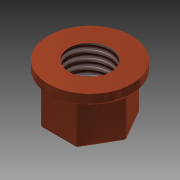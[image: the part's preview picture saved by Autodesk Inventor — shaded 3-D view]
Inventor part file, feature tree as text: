
AUTODESK INVENTOR PART (.ipt)
format: ipt  version: 2015 (Build 190159000, 159)  size: 140,800 bytes
history: native  units: mm
features: extrude x2, sketch x2, thread x1, fillet x1, chamfer x1
ambient origin geometry x8: Origin, YZ Plane, XZ Plane, XY Plane, X Axis, Y Axis, Z Axis, Center Point
bodies: 实体1 (feature_tree)
feature tree (7):
  extrude  "拉伸1"  Depth=4.0mm
  extrude  "拉伸2"  Depth=4.0mm TaperAngle=0.0deg
  thread  "螺纹1"  [1 undecoded]
  fillet  "圆角1"  Radius=4.0mm
  chamfer  "倒角1"  Distance=1.0mm
  sketch  "草图1"  dims[d0=4.0mm d1=1.076513mm]
  sketch  "草图2"  dims[d2=6.0mm d3=4.0mm d4=0.0mm d5=8.0mm d6=4.0mm d7=1.0mm d8=0.0mm d9=10.0mm d10=0.0mm d11=0.25mm d12=0.25mm d13=2.0mm d14=45.0deg]
note: 1 required parameter value undecoded (feature->parameter linkage not recoverable at this tier; creation-order binding heuristic only, values carry confidence <= 0.55)
